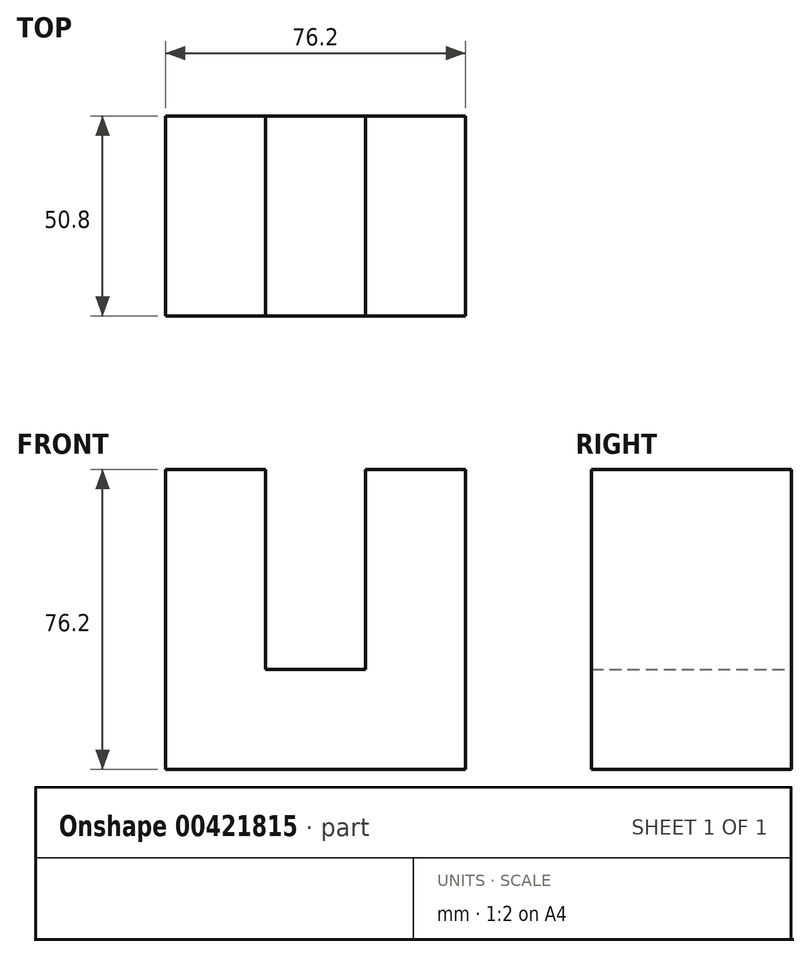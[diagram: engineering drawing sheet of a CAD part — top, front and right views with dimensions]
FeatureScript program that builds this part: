
annotation { "Feature Type Name" : "Feature", "Feature Type Description" : "" }
export const myFeature = defineFeature(function(context is Context, id is Id, definition is map)
    precondition{}
    {
        {
            var Q0;
            Q0=qCreatedBy(makeId("Front.planeOp"),FACE);
            var sketch = newSketch(context, id + "F0", { "sketchPlane" : qUnion([Q0])});
            skLineSegment(sketch, "E0", {"start": v(29.8, 0) * mm, "end": v(-46.4, 0) * mm});
            skLineSegment(sketch, "E1", {"start": v(-46.4, 0) * mm, "end": v(-46.4, 76.2) * mm});
            skLineSegment(sketch, "E2", {"start": v(-46.4, 76.2) * mm, "end": v(-21, 76.2) * mm});
            skLineSegment(sketch, "E3", {"start": v(-21, 76.2) * mm, "end": v(-21, 25.4) * mm});
            skLineSegment(sketch, "E4", {"start": v(-21, 25.4) * mm, "end": v(4.4, 25.4) * mm});
            skLineSegment(sketch, "E5", {"start": v(4.4, 25.4) * mm, "end": v(4.4, 76.2) * mm});
            skLineSegment(sketch, "E6", {"start": v(4.4, 76.2) * mm, "end": v(29.8, 76.2) * mm});
            skLineSegment(sketch, "E7", {"start": v(29.8, 76.2) * mm, "end": v(29.8, 0) * mm});
            skSolve(sketch);
        }
        {
            var Q0;
            Q0 = qSketchRegion(id + "F0", true);
            extrude(context, id + "F1", {"entities" : qUnion([Q0]), "depth" : 50.8 * mm});
        }
    });
